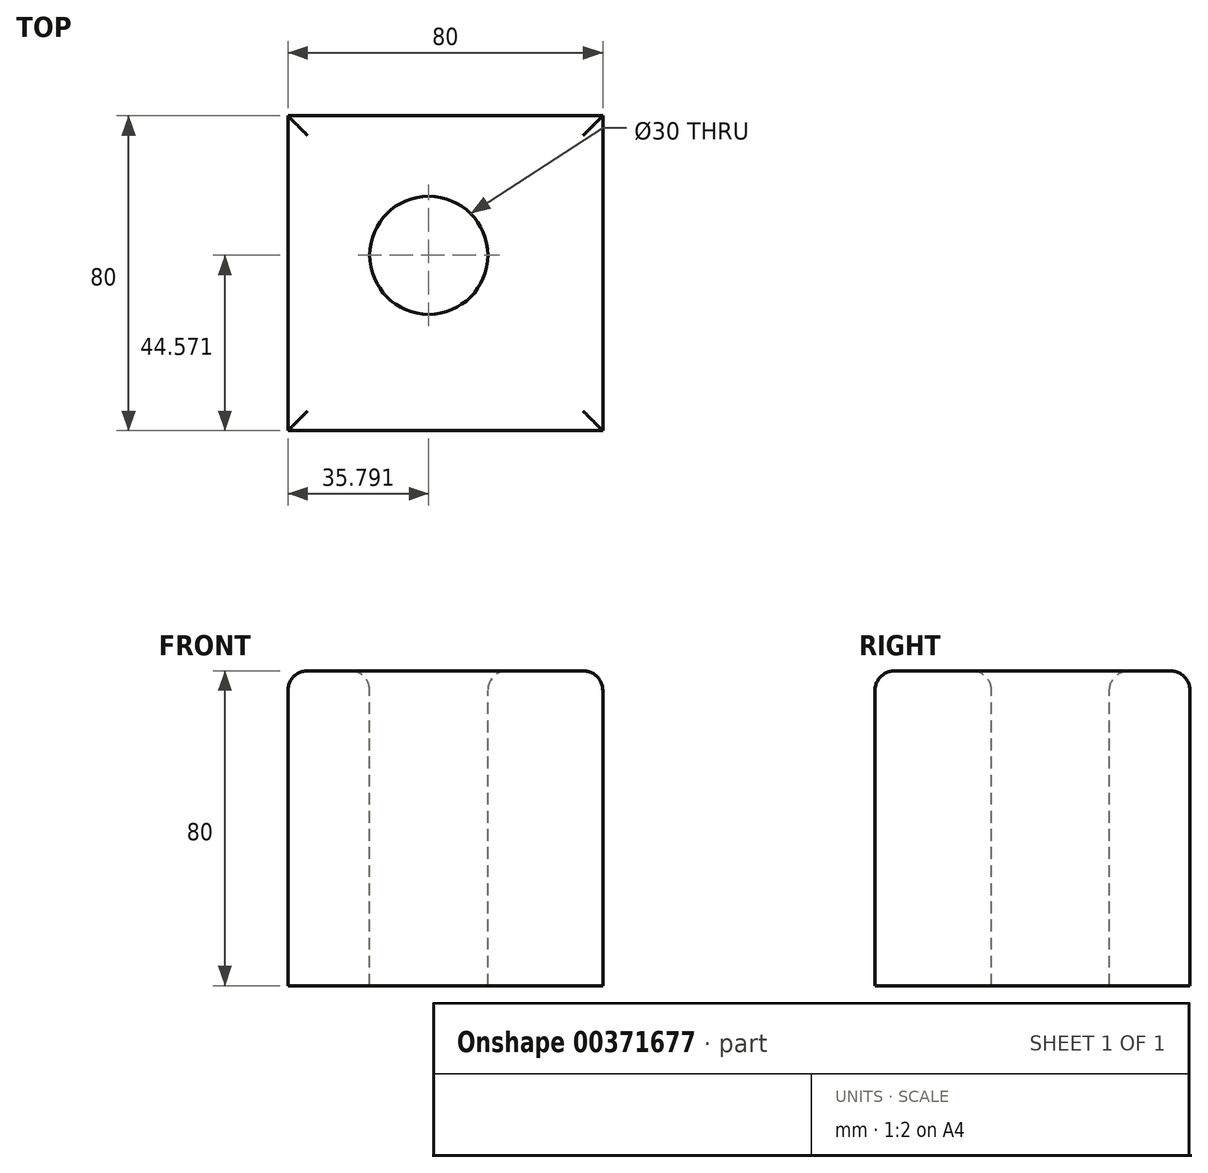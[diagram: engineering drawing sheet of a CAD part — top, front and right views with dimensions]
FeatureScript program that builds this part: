
annotation { "Feature Type Name" : "Feature", "Feature Type Description" : "" }
export const myFeature = defineFeature(function(context is Context, id is Id, definition is map)
    precondition{}
    {
        {
            var Q0;
            Q0=qCreatedBy(makeId("Top.planeOp"),FACE);
            var sketch = newSketch(context, id + "F0", { "sketchPlane" : qUnion([Q0])});
            skLineSegment(sketch, "E0.bottom", {"start": v(4.28, -19.12) * mm, "end": v(-75.72, -19.12) * mm});
            skLineSegment(sketch, "E0.top", {"start": v(4.28, 60.88) * mm, "end": v(-75.72, 60.88) * mm});
            skLineSegment(sketch, "E0.left", {"start": v(4.28, -19.12) * mm, "end": v(4.28, 60.88) * mm});
            skLineSegment(sketch, "E0.right", {"start": v(-75.72, -19.12) * mm, "end": v(-75.72, 60.88) * mm});
            skPoint(sketch, "E0.middle", {"position": v(-35.72, 20.88) * mm});
            skSolve(sketch);
        }
        {
            var Q0;
            Q0=makeQuery(id+"F0.imprint","IMPRINT",FACE,{"disambiguationData":[TD([[makeQuery(id+"F0.imprint","IMPRINT",EDGE,{"derivedFrom":sQuery(id+"F0.wireOp",EDGE,"E0.bottom")}),-1.0]])]});
            extrude(context, id + "F1", {"entities" : qUnion([Q0]), "depth" : 80 * mm});
        }
        {
            var Q0;
            Q0=makeQuery(id+"F1.opExtrude","CAP_FACE",FACE,{"disambiguationData":[OSD([sQuery(id+"F0.wireOp",EDGE,"E0.bottom"),sQuery(id+"F0.wireOp",EDGE,"E0.top"),sQuery(id+"F0.wireOp",EDGE,"E0.left"),sQuery(id+"F0.wireOp",EDGE,"E0.right")])],"isStart":false});
            var sketch = newSketch(context, id + "F2", { "sketchPlane" : qUnion([Q0])});
            skCircle(sketch, "E1", {"center": v(-39.93, 25.45) * mm, "radius": 15 * mm});
            skSolve(sketch);
        }
        {
            var Q0;
            Q0=makeQuery(id+"F2.imprint","IMPRINT",FACE,{"disambiguationData":[TD([[makeQuery(id+"F2.imprint","IMPRINT",EDGE,{"derivedFrom":sQuery(id+"F2.wireOp",EDGE,"E1")}),1.0]])]});
            extrude(context, id + "F3", {"entities" : qUnion([Q0]), "operationType" : NewBodyOperationType.REMOVE, "endBound" : BoundingType.THROUGH_ALL, "oppositeDirection" : true, "depth" : 25 * mm});
        }
        {
            var Q0;
            Q0=makeQuery(id+"F1.opExtrude","CAP_FACE",FACE,{"disambiguationData":[OSD([sQuery(id+"F0.wireOp",EDGE,"E0.bottom"),sQuery(id+"F0.wireOp",EDGE,"E0.top"),sQuery(id+"F0.wireOp",EDGE,"E0.left"),sQuery(id+"F0.wireOp",EDGE,"E0.right")])],"isStart":false});
            var Q1;
            Q1=makeQuery(id+"F3.boolean.opBoolean","COPY",EDGE,{"derivedFrom":makeQuery(id+"F3.opExtrude","CAP_EDGE",EDGE,{"disambiguationData":[OSD([sQuery(id+"F2.wireOp",EDGE,"E1")])],"isStart":true})});
            var Q2;
            Q2=makeQuery(id+"F1.opExtrude","CAP_EDGE",EDGE,{"disambiguationData":[OSD([sQuery(id+"F0.wireOp",EDGE,"E0.right")])],"isStart":false});
            fillet(context, id + "F4", {"entities" : qUnion([Q0, Q1, Q2]), "radius" : 5 * mm, "tangentPropagation" : true, "allowEdgeOverflow" : false});
        }
    });
